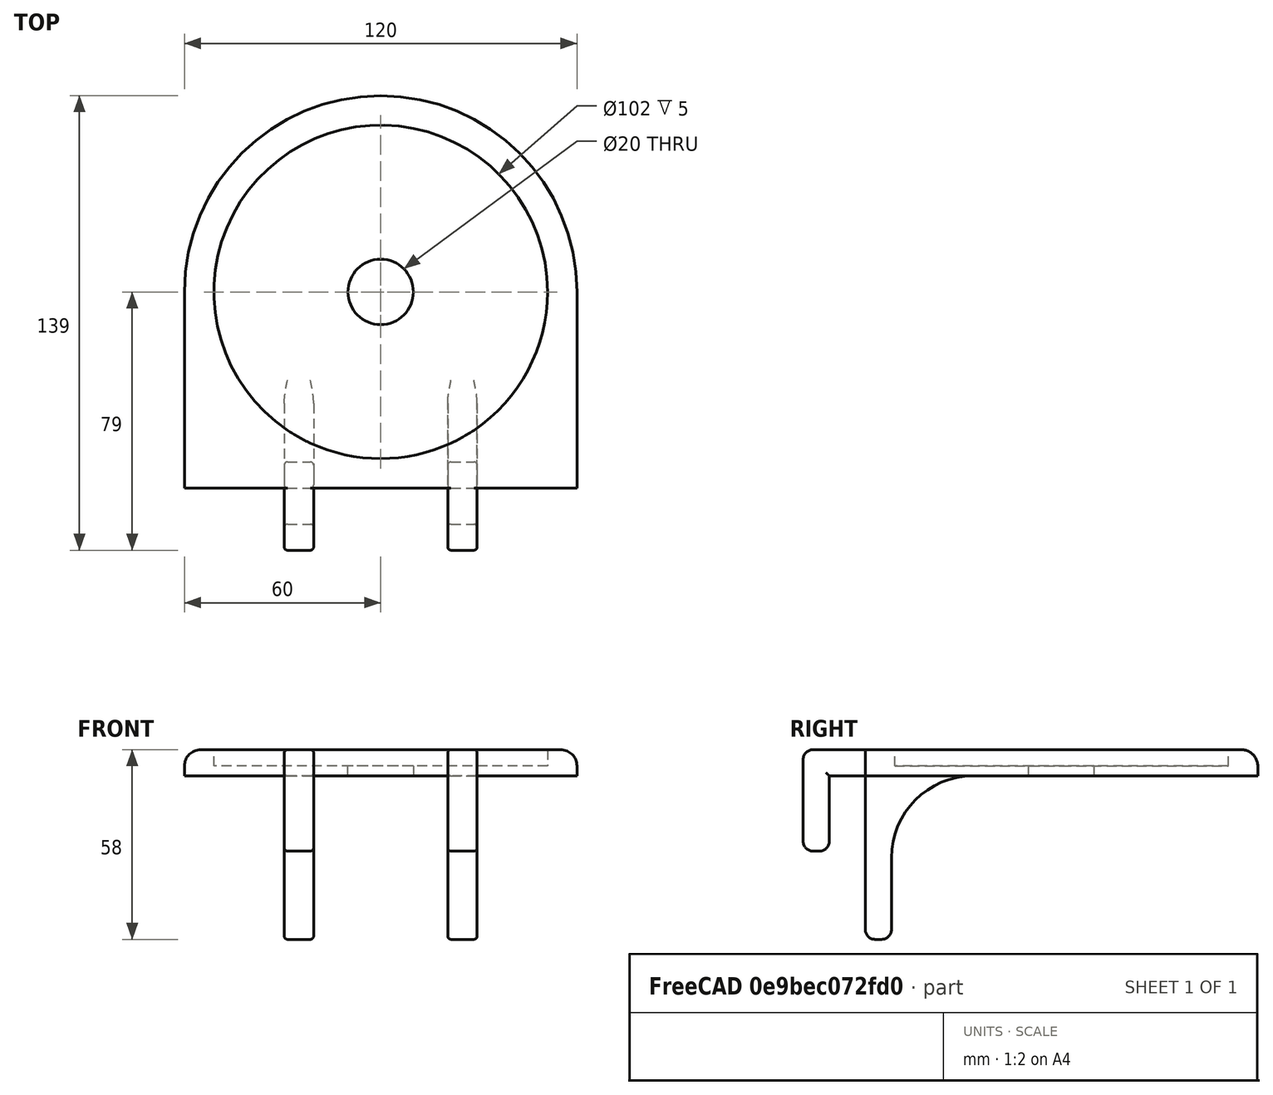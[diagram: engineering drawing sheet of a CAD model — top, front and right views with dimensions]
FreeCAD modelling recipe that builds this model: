
FCSTD DOCUMENT  (FreeCAD 0.21R33668 +7 (Git))
Label: DollStand
License: All rights reserved
LicenseURL: http://en.wikipedia.org/wiki/All_rights_reserved
objects: Sketcher::SketchObject×4, PartDesign::Body×3, PartDesign::Pad×2, PartDesign::Fillet×2, PartDesign::Pocket×2, App::Link×1, App::LinkGroup×1, Part::MultiFuse×1, PartDesign::FeatureBase×1, App::Part×1, Mesh::Feature×1
note: 21 computed .brp shape members not serialized (recipe doc carries the construction recipe); baked Part::Feature solids carry a one-line shape summary decoded from their .brp

FEATURE [Sketcher::SketchObject] Sketch  label="HookSketch"
  FullyConstrained = true
  MapMode = 5
  Placement = pos=(0,0,0) rot=(0.57735,0.57735,0.57735;2.0944rad)
  Support = -> [YZ_Plane001]
  sketch-geometry (28):
    g0: LineSegment StartX=3 StartY=0 StartZ=0 EndX=66 EndY=0 EndZ=0
    g1: LineSegment StartX=69 StartY=-3 StartZ=0 EndX=69 EndY=-5 EndZ=0
    g2: LineSegment StartX=66 StartY=-8 StartZ=0 EndX=52 EndY=-8 EndZ=0
    g3: LineSegment StartX=27 StartY=-33 StartZ=0 EndX=27 EndY=-55 EndZ=0
    g4: LineSegment StartX=24 StartY=-58 StartZ=0 EndX=22 EndY=-58 EndZ=0
    g5: LineSegment StartX=19 StartY=-55 StartZ=0 EndX=19 EndY=-8 EndZ=0
    g6: LineSegment StartX=19 StartY=-8 StartZ=0 EndX=8 EndY=-8 EndZ=0
    g7: LineSegment StartX=8 StartY=-8 StartZ=0 EndX=8 EndY=-28 EndZ=0
    g8: LineSegment StartX=5 StartY=-31 StartZ=0 EndX=3 EndY=-31 EndZ=0
    g9: LineSegment StartX=0 StartY=-28 StartZ=0 EndX=0 EndY=-3 EndZ=0
    g10: ArcOfCircle CenterX=3 CenterY=-3 CenterZ=0 NormalX=0 NormalY=0 NormalZ=1 AngleXU=0 Radius=3 StartAngle=1.5708 EndAngle=3.14159
    g11: GeomPoint X=0 Y=0 Z=0
    g12: ArcOfCircle CenterX=66 CenterY=-3 CenterZ=0 NormalX=0 NormalY=0 NormalZ=1 AngleXU=0 Radius=3 StartAngle=0 EndAngle=1.5708
    g13: GeomPoint X=69 Y=0 Z=0
    g14: ArcOfCircle CenterX=66 CenterY=-5 CenterZ=0 NormalX=0 NormalY=0 NormalZ=1 AngleXU=0 Radius=3 StartAngle=4.71239 EndAngle=6.28319
    g15: GeomPoint X=69 Y=-8 Z=0
    g16: ArcOfCircle CenterX=52 CenterY=-33 CenterZ=0 NormalX=0 NormalY=0 NormalZ=1 AngleXU=0 Radius=25 StartAngle=1.5708 EndAngle=3.14159
    g17: GeomPoint X=27 Y=-8 Z=0
    g18: ArcOfCircle CenterX=24 CenterY=-55 CenterZ=0 NormalX=0 NormalY=0 NormalZ=1 AngleXU=0 Radius=3 StartAngle=4.71239 EndAngle=6.28319
    g19: GeomPoint X=27 Y=-58 Z=0
    g20: ArcOfCircle CenterX=22 CenterY=-55 CenterZ=0 NormalX=0 NormalY=0 NormalZ=1 AngleXU=0 Radius=3 StartAngle=3.14159 EndAngle=4.71239
    g21: GeomPoint X=19 Y=-58 Z=0
    g22: GeomPoint X=19 Y=-8 Z=0
    g23: GeomPoint X=8 Y=-8 Z=0
    g24: ArcOfCircle CenterX=5 CenterY=-28 CenterZ=0 NormalX=0 NormalY=0 NormalZ=1 AngleXU=0 Radius=3 StartAngle=4.71239 EndAngle=6.28319
    g25: GeomPoint X=8 Y=-31 Z=0
    g26: ArcOfCircle CenterX=3 CenterY=-28 CenterZ=0 NormalX=0 NormalY=0 NormalZ=1 AngleXU=0 Radius=3 StartAngle=3.14159 EndAngle=4.71239
    g27: GeomPoint X=0 Y=-31 Z=0
  constraints (64):
    c: Coincident(g-1,g11)
    c: PointOnObject(g13,g-1)
    c: Vertical(g1)
    c: Horizontal(g2)
    c: Vertical(g3)
    c: Horizontal(g4)
    c: Vertical(g5)
    c: Horizontal(g6)
    c: Vertical(g7)
    c: PointOnObject(g27,g-2)
    c: Horizontal(g8)
    c: DistanceX(g21,g19) = 8
    c: DistanceX(g27,g25) = 8
    c: DistanceY(g19,g17) = 50
    c: DistanceY(g25,g23) = 23
    c: DistanceY(g15,g13) = 8
    c: DistanceY(g27,g11) = 31
    c: PointOnObject(g11,g9)
    c: PointOnObject(g11,g0)
    c: Tangent(g9,g10) = 1.5708
    c: Tangent(g0,g10) = 1.5708
    c: PointOnObject(g13,g0)
    c: PointOnObject(g13,g1)
    c: Tangent(g0,g12) = 1.5708
    c: Tangent(g1,g12) = 1.5708
    c: PointOnObject(g15,g1)
    c: PointOnObject(g15,g2)
    c: Tangent(g1,g14) = 1.5708
    c: Tangent(g2,g14) = 1.5708
    c: PointOnObject(g17,g2)
    c: PointOnObject(g17,g3)
    c: Tangent(g2,g16) = -1.5708
    c: Tangent(g3,g16) = -1.5708
    c: PointOnObject(g19,g3)
    c: PointOnObject(g19,g4)
    c: Tangent(g3,g18) = 1.5708
    c: Tangent(g4,g18) = 1.5708
    c: PointOnObject(g21,g4)
    c: PointOnObject(g21,g5)
    c: Tangent(g4,g20) = 1.5708
    c: Tangent(g5,g20) = 1.5708
    c: PointOnObject(g22,g5)
    c: PointOnObject(g22,g6)
    c: PointOnObject(g25,g7)
    c: PointOnObject(g25,g8)
    c: Tangent(g7,g24) = 1.5708
    c: Tangent(g8,g24) = 1.5708
    c: PointOnObject(g27,g8)
    c: PointOnObject(g27,g9)
    c: Tangent(g8,g26) = 1.5708
    c: Tangent(g9,g26) = 1.5708
    c: Equal(g10,g12)
    c: Equal(g10,g14)
    c: Equal(g10,g18)
    c: Equal(g10,g20)
    c: Equal(g10,g24)
    c: Equal(g10,g26)
    c: Radius(g10) = 3
    c: Radius(g16) = 25
    c: DistanceX(g6,g6) = 11
    c: Coincident(g7,g23)
    c: Coincident(g5,g6)
    c: Coincident(g7,g6)
    c: DistanceX(g5,g1) = 50
FEATURE [PartDesign::Pad] Pad  label="HookPad"
  Direction = (1,-2e-16,3e-16)
  Length = 9
  Length2 = 10
  Midplane = true
  Placement = pos=(0,0,0) rot=(0.57735,0.57735,0.57735;2.0944rad)
  Profile = -> Sketch
  ReferenceAxis = -> Sketch [N_Axis]
  Type = 0
FEATURE [PartDesign::Fillet] Fillet  label="HookBodyFillet"
  Base = -> Pad [Face20,Face19]
  BaseFeature = -> Pad
  Placement = pos=(0,0,0) rot=(0.57735,0.57735,0.57735;2.0944rad)
  Radius = 1
  SupportTransform = false
  UseAllEdges = false
FEATURE [PartDesign::Body] Body  label="HookBody"
  Group = -> [Sketch,Pad,Fillet]
  Origin = -> Origin001
  Placement = pos=(-25,0,0) rot=(0,0,1;0rad)
  Tip = -> Fillet
FEATURE [Sketcher::SketchObject] Sketch001  label="PlateauBodySketch"
  FullyConstrained = true
  MapMode = 5
  Support = -> [XY_Plane002]
  sketch-geometry (4):
    g0: ArcOfCircle CenterX=0 CenterY=79 CenterZ=0 NormalX=0 NormalY=0 NormalZ=1 AngleXU=0 Radius=60 StartAngle=0 EndAngle=3.14159
    g1: LineSegment StartX=-60 StartY=79 StartZ=0 EndX=-60 EndY=19 EndZ=0
    g2: LineSegment StartX=-60 StartY=19 StartZ=0 EndX=60 EndY=19 EndZ=0
    g3: LineSegment StartX=60 StartY=19 StartZ=0 EndX=60 EndY=79 EndZ=0
  constraints (12):
    c: PointOnObject(g0,g-2)
    c: Horizontal(g0,g0)
    c: Horizontal(g0,g0)
    c: Tangent(g0,g1) = -1.5708
    c: Coincident(g1,g2)
    c: Horizontal(g2)
    c: Coincident(g2,g3)
    c: Coincident(g3,g0)
    c: Vertical(g3)
    c: Diameter(g0) = 120
    c: DistanceY(g-1,g1) = 19
    c: DistanceY(g1,g1) = 60
FEATURE [App::Link] Link  label="HookBody001"
  LinkTransform = true
  LinkedObject = -> Body
FEATURE [App::LinkGroup] LinkGroup
  ElementList = -> [Link]
  LinkMode = 1
  Placement = pos=(50,0,0) rot=(0,0,1;0rad)
FEATURE [PartDesign::Pad] Pad001  label="PlateauPad"
  Direction = (0,0,1)
  Length = 8
  Length2 = 10
  Profile = -> Sketch001
  ReferenceAxis = -> Sketch001 [N_Axis]
  Reversed = true
  Type = 0
FEATURE [PartDesign::Body] Body001  label="PlateauBody"
  Group = -> [Sketch001,Pad001]
  Origin = -> Origin002
  Tip = -> Pad001
FEATURE [Part::MultiFuse] Fusion
  Shapes = -> [Body,Body001,LinkGroup]
FEATURE [Sketcher::SketchObject] Sketch002  label="HoleSketch"
  FullyConstrained = true
  MapMode = 2
  Support = -> [Fusion]
  sketch-geometry (1):
    g0: Circle CenterX=0 CenterY=79 CenterZ=0 NormalX=0 NormalY=0 NormalZ=1 AngleXU=0 Radius=51
  constraints (3):
    c: PointOnObject(g0,g-2)
    c: Diameter(g0) = 102
    c: DistanceY(g-1,g0) = 79
FEATURE [PartDesign::FeatureBase] BaseFeature
  BaseFeature = -> Fusion
FEATURE [PartDesign::Pocket] Pocket
  BaseFeature = -> BaseFeature
  Direction = (0,0,-1)
  Length = 5
  Length2 = 5
  Profile = -> Sketch002
  ReferenceAxis = -> Sketch002 [N_Axis]
  Type = 0
FEATURE [Sketcher::SketchObject] Sketch003  label="EasyRemovalHole"
  ExternalGeometry = -> [Pocket]
  FullyConstrained = true
  MapMode = 5
  Placement = pos=(0,0,-5) rot=(0,0,1;0rad)
  Support = -> [Pocket]
  sketch-geometry (1):
    g0: Circle CenterX=0 CenterY=79 CenterZ=0 NormalX=0 NormalY=0 NormalZ=1 AngleXU=0 Radius=10
  constraints (2):
    c: Coincident(g0,g-3)
    c: Diameter(g0) = 20
FEATURE [PartDesign::Pocket] Pocket001
  BaseFeature = -> Pocket
  Direction = (0,0,-1)
  Length = 5
  Length2 = 5
  Profile = -> Sketch003
  ReferenceAxis = -> Sketch003 [N_Axis]
  Type = 1
FEATURE [PartDesign::Fillet] Fillet001
  Base = -> Pocket001 [Edge77,Edge76,Edge78]
  BaseFeature = -> Pocket001
  Radius = 5
  SupportTransform = false
  UseAllEdges = false
FEATURE [PartDesign::Body] Body002  label="Body"
  BaseFeature = -> Fusion
  Group = -> [BaseFeature,Sketch002,Sketch003,Pocket,Pocket001,Fillet001]
  Origin = -> Origin003
  Tip = -> Fillet001
FEATURE [App::Part] Part  label="DollStandPart"
  Group = -> [Body002]
  Origin = -> Origin
FEATURE [Mesh::Feature] Mesh  label="DollStandPart (Meshed)"
